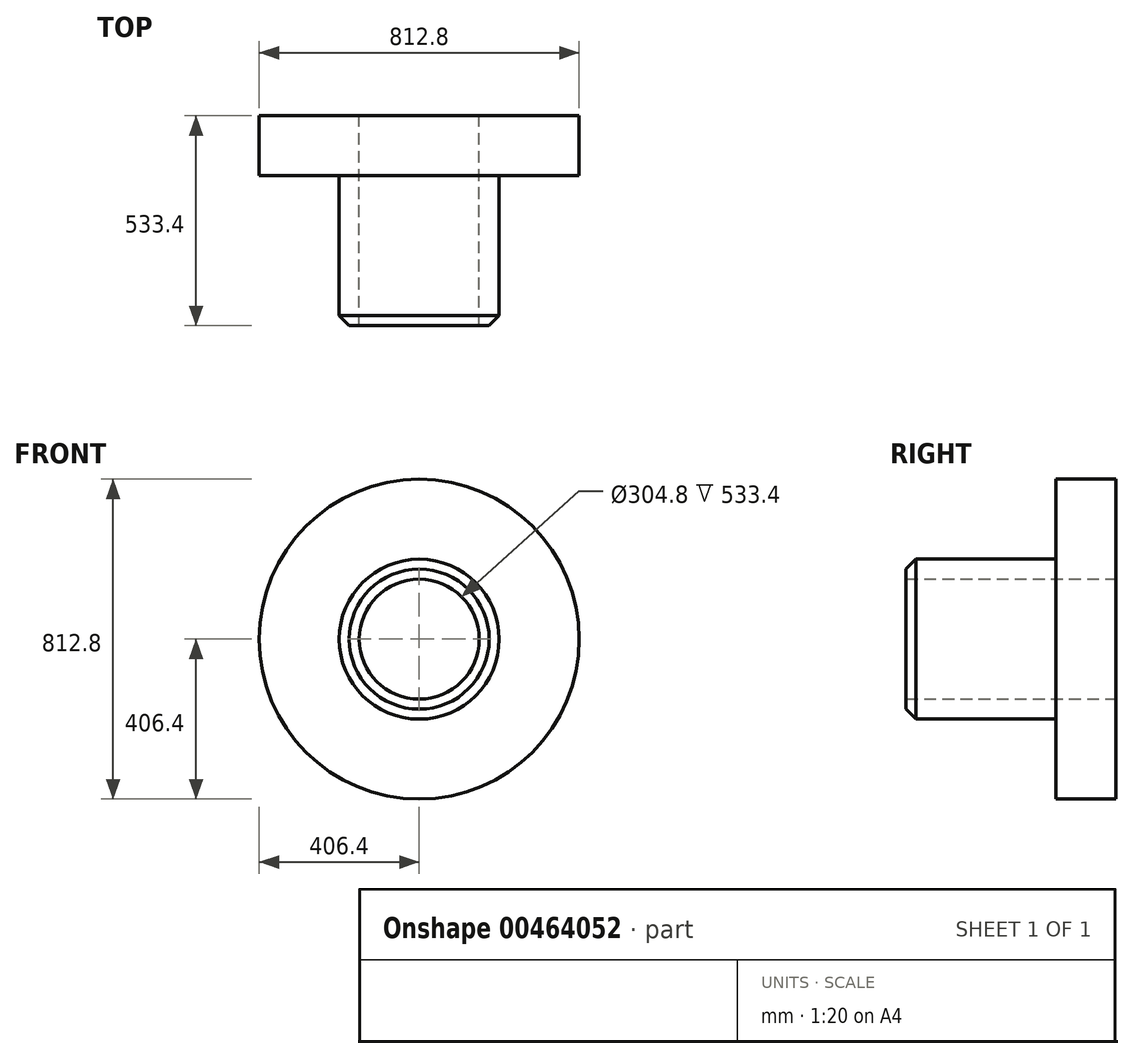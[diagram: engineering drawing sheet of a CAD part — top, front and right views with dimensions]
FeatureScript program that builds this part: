
annotation { "Feature Type Name" : "Feature", "Feature Type Description" : "" }
export const myFeature = defineFeature(function(context is Context, id is Id, definition is map)
    precondition{}
    {
        {
            var Q0;
            Q0=qCreatedBy(makeId("Front.planeOp"),FACE);
            var sketch = newSketch(context, id + "F0", { "sketchPlane" : qUnion([Q0])});
            skCircle(sketch, "E0", {"center": v(0, 0) * mm, "radius": 406.4 * mm});
            skCircle(sketch, "E1", {"center": v(0, 0) * mm, "radius": 203.2 * mm});
            skCircle(sketch, "E2", {"center": v(0, 0) * mm, "radius": 152.4 * mm});
            skSolve(sketch);
        }
        {
            var Q0;
            Q0 = qSketchRegion(id + "F0", true);
            extrude(context, id + "F1", {"entities" : qUnion([Q0]), "depth" : 152.4 * mm, "symmetric" : true});
        }
        {
            var Q0;
            Q0=makeQuery(id+"F0.imprint","IMPRINT",FACE,{"disambiguationData":[TD([[makeQuery(id+"F0.imprint","IMPRINT",EDGE,{"derivedFrom":sQuery(id+"F0.wireOp",EDGE,"E1")}),1.0]])]});
            extrude(context, id + "F2", {"entities" : qUnion([Q0]), "operationType" : NewBodyOperationType.ADD, "depth" : 457.2 * mm});
        }
        {
            var Q0;
            Q0=makeQuery(id+"F0.imprint","IMPRINT",FACE,{"disambiguationData":[TD([[makeQuery(id+"F0.imprint","IMPRINT",EDGE,{"derivedFrom":sQuery(id+"F0.wireOp",EDGE,"E2")}),1.0]])]});
            extrude(context, id + "F3", {"entities" : qUnion([Q0]), "operationType" : NewBodyOperationType.REMOVE, "oppositeDirection" : true, "depth" : 754.38 * mm});
        }
        {
            var Q0;
            Q0=makeQuery(id+"F2.opExtrude","CAP_EDGE",EDGE,{"disambiguationData":[OSD([sQuery(id+"F0.wireOp",EDGE,"E1")])],"isStart":false});
            chamfer(context, id + "F4", {"entities" : qUnion([Q0]), "width" : 25.4 * mm, "tangentPropagation" : true});
        }
        {
            var Q0;
            Q0=makeQuery(id+"F2.opExtrude","CAP_FACE",FACE,{"disambiguationData":[OSD([sQuery(id+"F0.wireOp",EDGE,"E1"),sQuery(id+"F0.wireOp",EDGE,"E2")])],"isStart":true});
            extrude(context, id + "F5", {"entities" : qUnion([Q0]), "operationType" : NewBodyOperationType.ADD, "depth" : 76.2 * mm});
        }
    });
